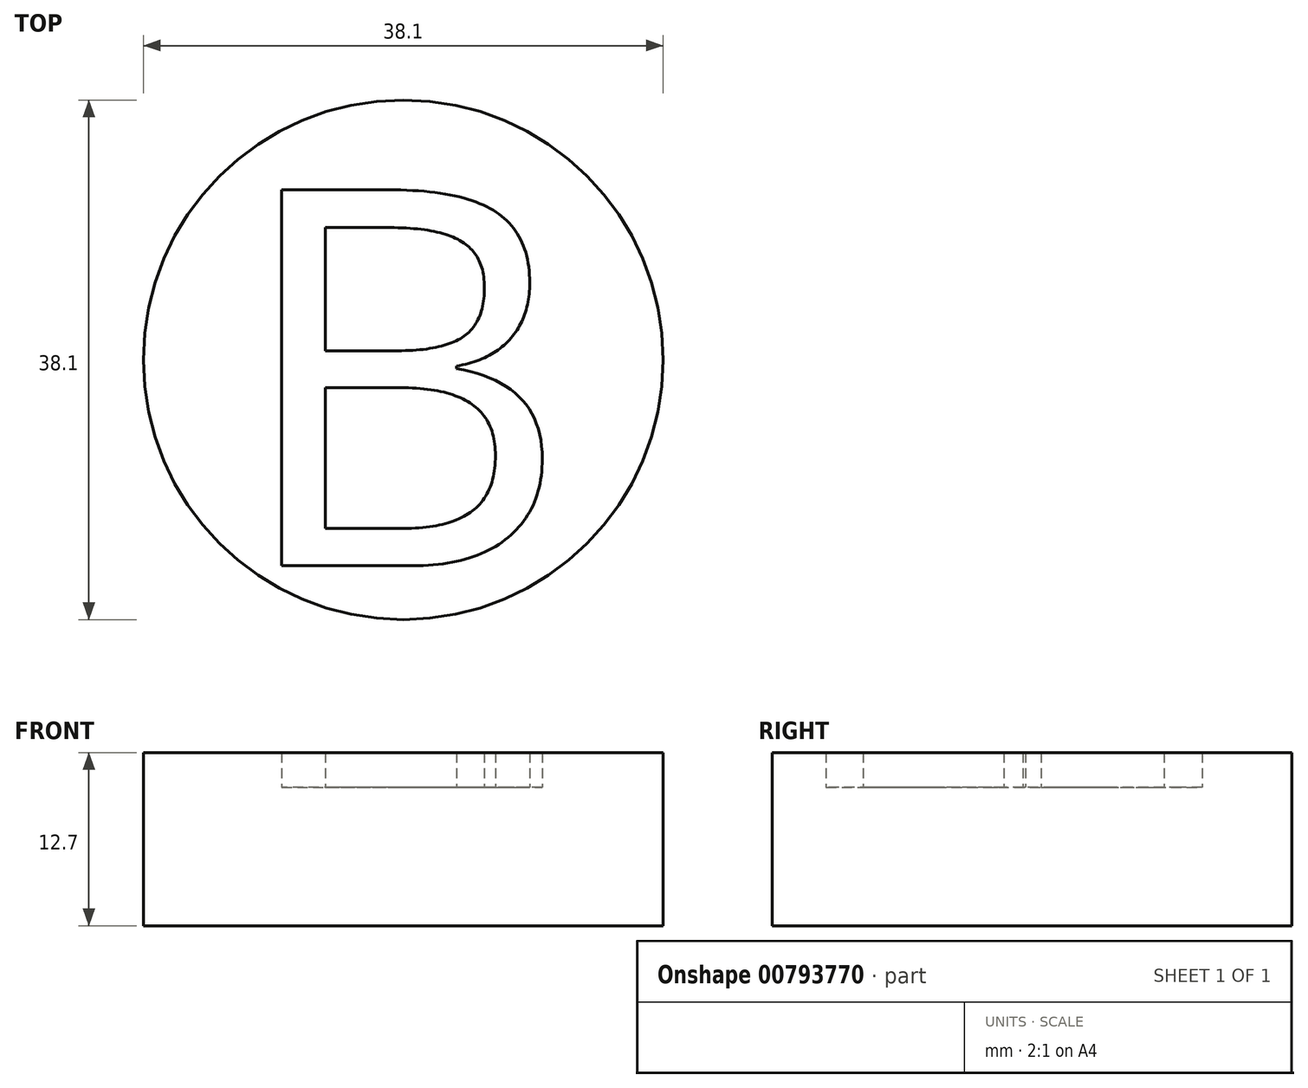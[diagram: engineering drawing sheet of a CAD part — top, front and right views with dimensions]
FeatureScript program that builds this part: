
annotation { "Feature Type Name" : "Feature", "Feature Type Description" : "" }
export const myFeature = defineFeature(function(context is Context, id is Id, definition is map)
    precondition{}
    {
        {
            var Q0;
            Q0=qCreatedBy(makeId("Top.planeOp"),FACE);
            var sketch = newSketch(context, id + "F0", { "sketchPlane" : qUnion([Q0])});
            skCircle(sketch, "E0", {"center": v(0, 0) * mm, "radius": 19.05 * mm});
            skSolve(sketch);
        }
        {
            var Q0;
            Q0 = qSketchRegion(id + "F0", true);
            extrude(context, id + "F1", {"entities" : qUnion([Q0]), "depth" : 12.7 * mm, "offsetDistance" : 25.4 * mm});
        }
        {
            var Q0;
            Q0=qCreatedBy(makeId("Top.planeOp"),FACE);
            var sketch = newSketch(context, id + "F2", { "sketchPlane" : qUnion([Q0])});
            skText(sketch, "E1", { "text": "B", "fontName": "OpenSans-Regular.ttf"});
            const initialGuessF2  = {"E1": [-0.0127, -0.0151, 1, 0, 0.0278]};
            skSetInitialGuess(sketch, initialGuessF2);
            skSolve(sketch);
        }
        {
            var Q0;
            Q0 = qSketchRegion(id + "F2", true);
            extrude(context, id + "F3", {"entities" : qUnion([Q0]), "operationType" : NewBodyOperationType.REMOVE, "depth" : 12.7 * mm, "offsetDistance" : 25.4 * mm, "hasSecondDirection" : true, "secondDirectionOppositeDirection" : false, "secondDirectionDepth" : 10.16 * mm});
        }
    });
